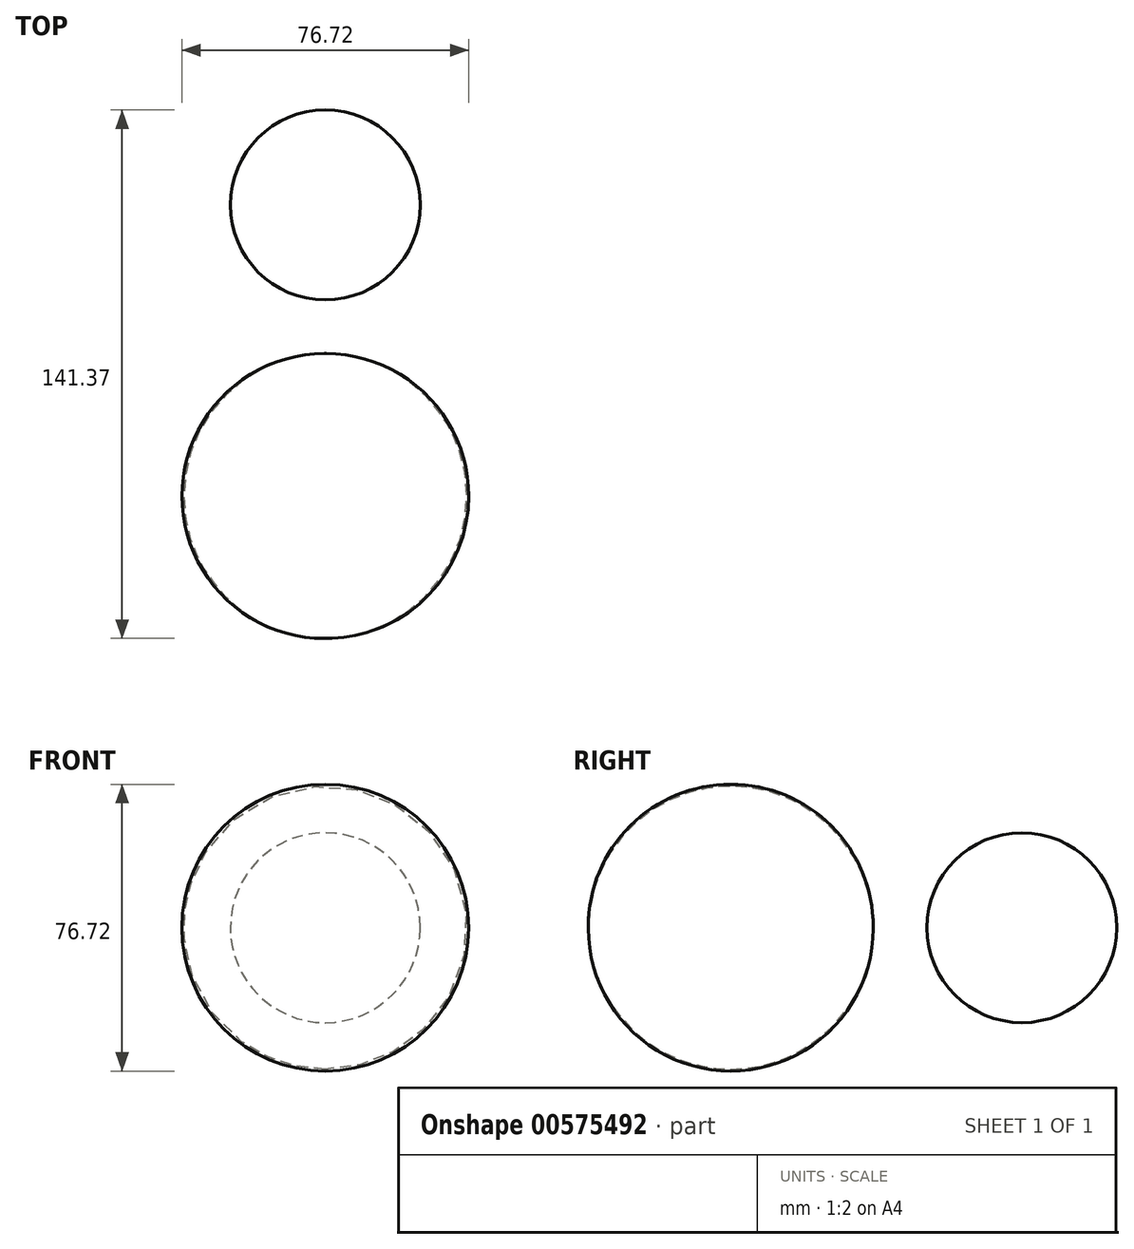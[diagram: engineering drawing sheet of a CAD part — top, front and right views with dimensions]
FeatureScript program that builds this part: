
annotation { "Feature Type Name" : "Feature", "Feature Type Description" : "" }
export const myFeature = defineFeature(function(context is Context, id is Id, definition is map)
    precondition{}
    {
        {
            var Q0;
            Q0=qCreatedBy(makeId("Top.planeOp"),FACE);
            var sketch = newSketch(context, id + "F0", { "sketchPlane" : qUnion([Q0])});
            skArc(sketch, "E0", {"start": v(0, 14.37) * mm, "mid": v(25.4, 39.77) * mm, "end": v(0, 65.17) * mm});
            skLineSegment(sketch, "E1", {"start": v(0, 14.37) * mm, "end": v(0, 65.17) * mm});
            skSolve(sketch);
        }
        {
            var Q0;
            Q0 = qSketchRegion(id + "F0", true);
            var Q1;
            Q1=sQuery(id+"F0.wireOp",EDGE,"E1");
            revolve(context, id + "F1", {"entities" : qUnion([Q0]), "axis" : qUnion([Q1]), "revolveType" : RevolveType.FULL});
        }
        {
            var Q0;
            Q0=qCreatedBy(makeId("Top.planeOp"),FACE);
            var sketch = newSketch(context, id + "F2", { "sketchPlane" : qUnion([Q0])});
            skArc(sketch, "E2", {"start": v(0, 0) * mm, "mid": v(-37.84, -38.1) * mm, "end": v(0, -76.2) * mm});
            skLineSegment(sketch, "E3", {"start": v(0, 0) * mm, "end": v(0, -76.2) * mm});
            skSolve(sketch);
        }
        {
            var Q0;
            Q0=makeQuery(id+"F2.imprint","IMPRINT",FACE,{"disambiguationData":[TD([[makeQuery(id+"F2.imprint","IMPRINT",EDGE,{"derivedFrom":sQuery(id+"F2.wireOp",EDGE,"E2")}),1.0]])]});
            var Q1;
            Q1=sQuery(id+"F2.wireOp",EDGE,"E3");
            revolve(context, id + "F3", {"entities" : qUnion([Q0]), "axis" : qUnion([Q1]), "revolveType" : RevolveType.FULL});
        }
    });
